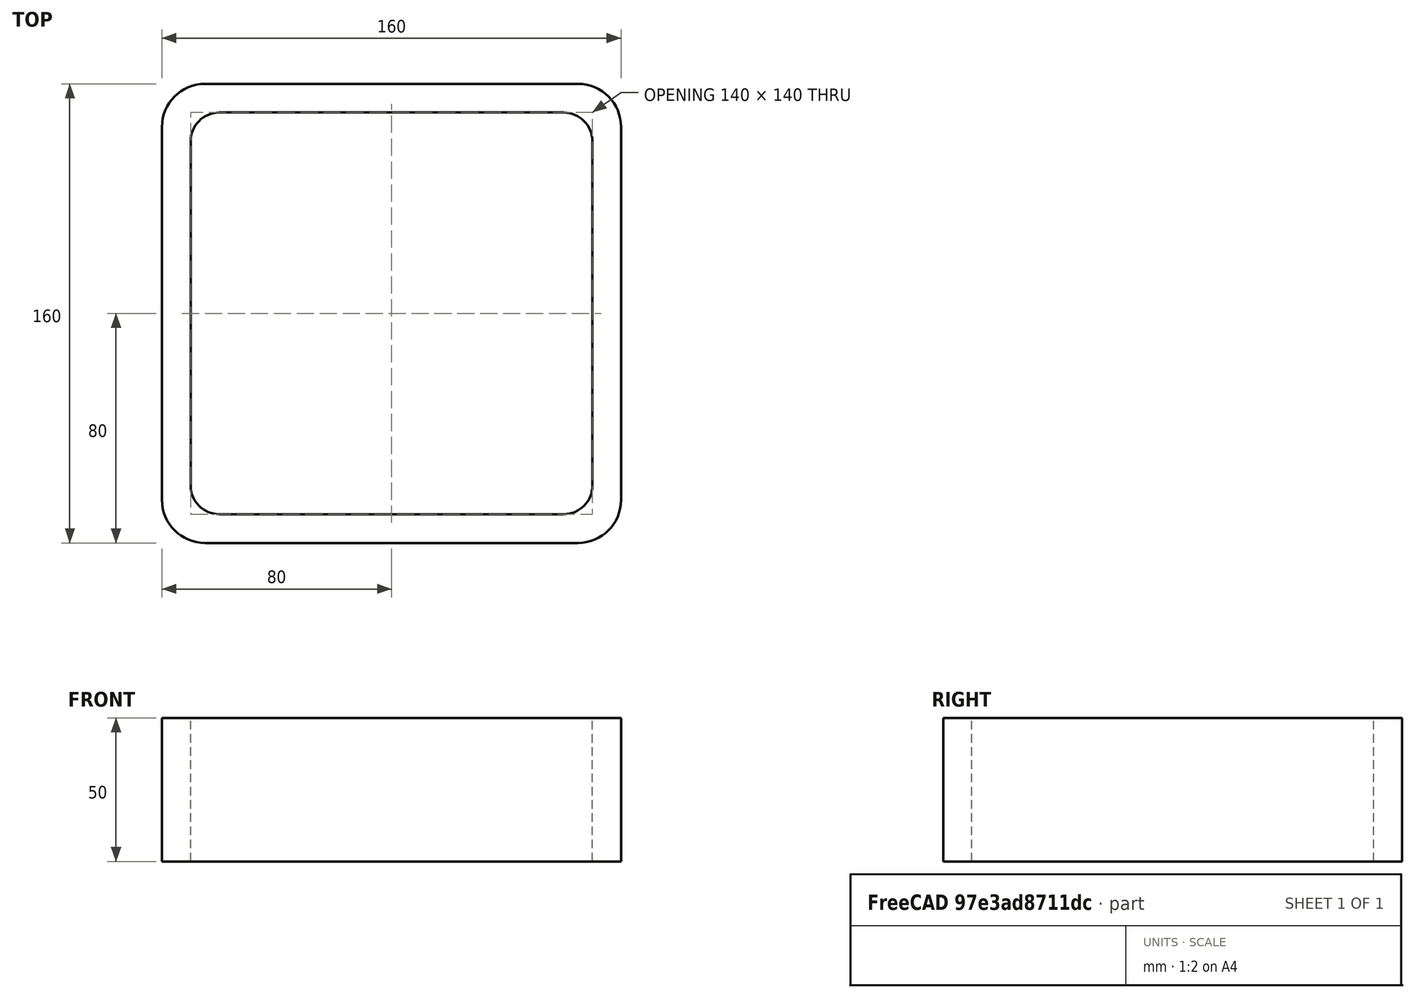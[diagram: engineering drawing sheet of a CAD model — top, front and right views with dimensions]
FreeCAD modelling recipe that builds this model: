
FCSTD DOCUMENT  (FreeCAD 0.15R4671 (Git))
Label: Square hollow section 160x160x10 EN10219 S235JRH
License: All rights reserved
LicenseURL: http://en.wikipedia.org/wiki/All_rights_reserved
objects: Sketcher::SketchObject×1, Part::Extrusion×1
note: 2 computed .brp shape members not serialized (recipe doc carries the construction recipe); baked Part::Feature solids carry a one-line shape summary decoded from their .brp

FEATURE [Sketcher::SketchObject] Sketch
  sketch-geometry (16):
    g0: LineSegment StartX=-60 StartY=70 StartZ=0 EndX=60 EndY=70 EndZ=0
    g1: LineSegment StartX=70 StartY=60 StartZ=0 EndX=70 EndY=-60 EndZ=0
    g2: LineSegment StartX=60 StartY=-70 StartZ=0 EndX=-60 EndY=-70 EndZ=0
    g3: LineSegment StartX=-70 StartY=-60 StartZ=0 EndX=-70 EndY=60 EndZ=0
    g4: LineSegment StartX=-65 StartY=80 StartZ=0 EndX=65 EndY=80 EndZ=0
    g5: LineSegment StartX=80 StartY=65 StartZ=0 EndX=80 EndY=-65 EndZ=0
    g6: LineSegment StartX=65 StartY=-80 StartZ=0 EndX=-65 EndY=-80 EndZ=0
    g7: LineSegment StartX=-80 StartY=-65 StartZ=0 EndX=-80 EndY=65 EndZ=0
    g8: ArcOfCircle CenterX=-60 CenterY=60 CenterZ=0 NormalX=0 NormalY=0 NormalZ=1 Radius=10 StartAngle=1.5708 EndAngle=3.14159
    g9: ArcOfCircle CenterX=60 CenterY=60 CenterZ=0 NormalX=0 NormalY=0 NormalZ=1 Radius=10 StartAngle=0 EndAngle=1.5708
    g10: ArcOfCircle CenterX=60 CenterY=-60 CenterZ=0 NormalX=0 NormalY=0 NormalZ=1 Radius=10 StartAngle=4.71239 EndAngle=6.28319
    g11: ArcOfCircle CenterX=-60 CenterY=-60 CenterZ=0 NormalX=0 NormalY=0 NormalZ=1 Radius=10 StartAngle=3.14159 EndAngle=4.71239
    g12: ArcOfCircle CenterX=65 CenterY=65 CenterZ=0 NormalX=0 NormalY=0 NormalZ=1 Radius=15 StartAngle=0 EndAngle=1.5708
    g13: ArcOfCircle CenterX=65 CenterY=-65 CenterZ=0 NormalX=0 NormalY=0 NormalZ=1 Radius=15 StartAngle=4.71239 EndAngle=6.28319
    g14: ArcOfCircle CenterX=-65 CenterY=-65 CenterZ=0 NormalX=0 NormalY=0 NormalZ=1 Radius=15 StartAngle=3.14159 EndAngle=4.71239
    g15: ArcOfCircle CenterX=-65 CenterY=65 CenterZ=0 NormalX=0 NormalY=0 NormalZ=1 Radius=15 StartAngle=1.5708 EndAngle=3.14159
  constraints (36):
    c: Horizontal(g2)
    c: Vertical(g3)
    c: Horizontal(g6)
    c: Vertical(g7)
    c: Tangent(g3,g8) = 1.5708
    c: Tangent(g0,g8) = 1.5708
    c: Tangent(g0,g9) = 1.5708
    c: Tangent(g1,g9) = 1.5708
    c: Tangent(g1,g10) = 1.5708
    c: Tangent(g2,g10) = 1.5708
    c: Tangent(g2,g11) = 1.5708
    c: Tangent(g3,g11) = 1.5708
    c: Tangent(g4,g12) = 1.5708
    c: Tangent(g5,g12) = 1.5708
    c: Tangent(g5,g13) = 1.5708
    c: Tangent(g6,g13) = 1.5708
    c: Tangent(g6,g14) = 1.5708
    c: Tangent(g7,g14) = 1.5708
    c: Tangent(g7,g15) = 1.5708
    c: Tangent(g4,g15) = 1.5708
    c: Equal(g9,g8)
    c: Equal(g9,g11)
    c: Equal(g9,g10)
    c: Equal(g12,g15)
    c: Equal(g12,g14)
    c: Equal(g12,g13)
    c: Symmetric(g4,g6,g-1)
    c: Symmetric(g7,g5,g-2)
    c: DistanceY(g4,g6) = -160
    c: DistanceX(g7,g5) = 160
    c: Symmetric(g3,g1,g-2)
    c: Symmetric(g0,g2,g-1)
    c: DistanceY(g0,g4) = 10
    c: DistanceX(g5,g1) = -10
    c: Radius(g9) = 10
    c: Radius(g12) = 15
FEATURE [Part::Extrusion] Extrude  label="Square hollow section 160x160x10 EN10219 S235JRH"
  Base = -> Sketch
  Dir = (0,0,50)
  Solid = true
